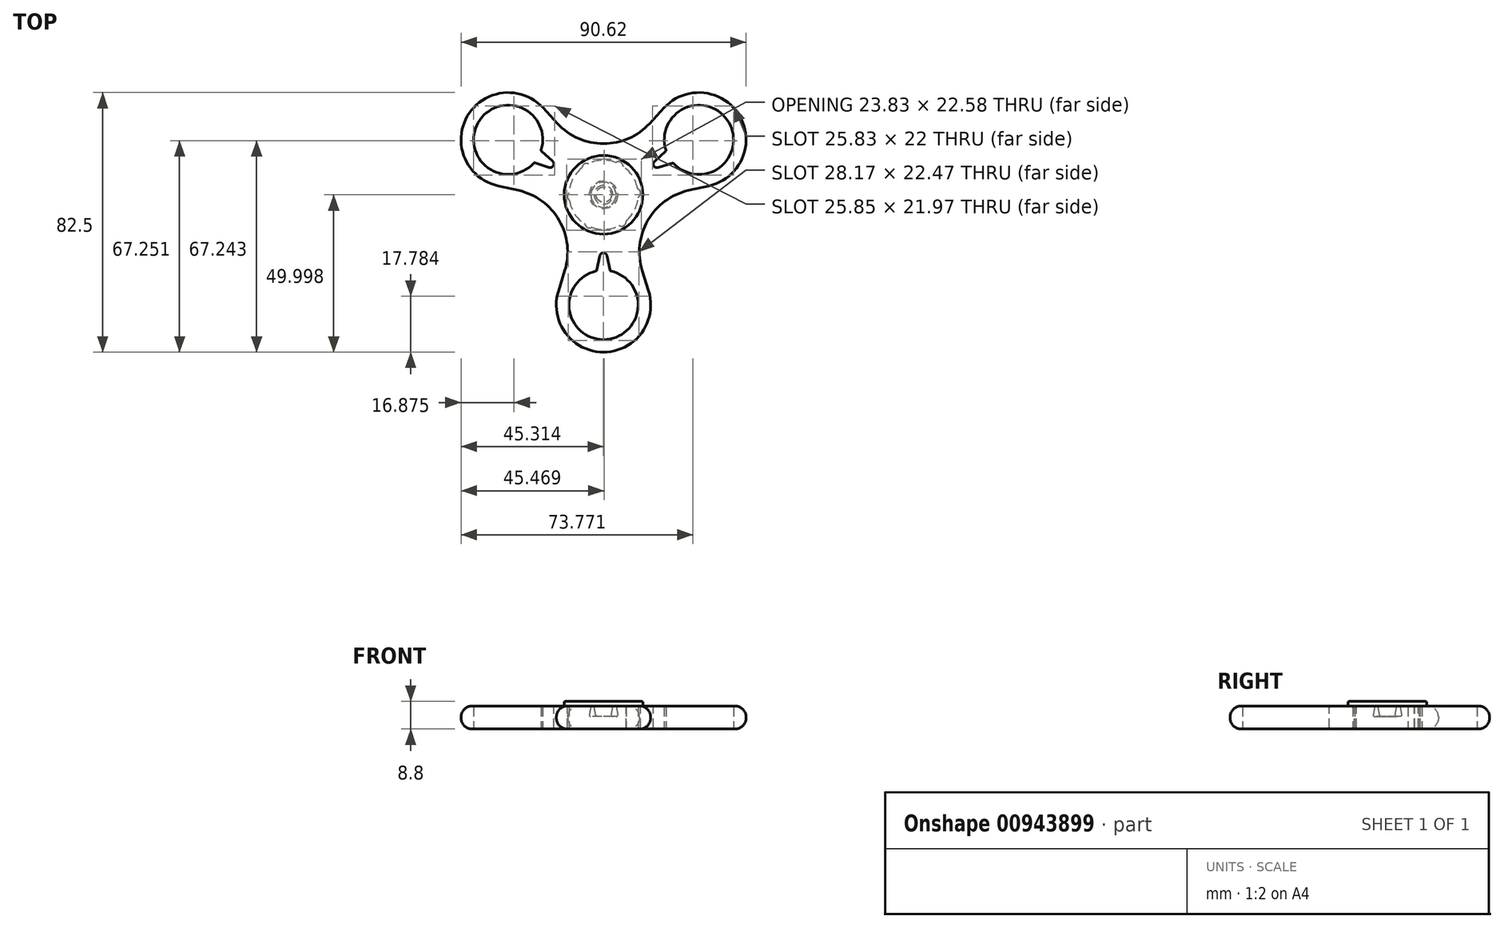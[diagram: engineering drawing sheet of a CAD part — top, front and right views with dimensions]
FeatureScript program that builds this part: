
annotation { "Feature Type Name" : "Feature", "Feature Type Description" : "" }
export const myFeature = defineFeature(function(context is Context, id is Id, definition is map)
    precondition{}
    {
        {
            var Q0;
            Q0=qCreatedBy(makeId("Top.planeOp"),FACE);
            var sketch = newSketch(context, id + "F0", { "sketchPlane" : qUnion([Q0])});
            skCircle(sketch, "E0", {"center": v(0, 0) * mm, "radius": 11 * mm});
            skCircle(sketch, "E1.cCircle", {"center": v(0, 0) * mm, "radius": 30.31 * mm, "construction": true});
            skLineSegment(sketch, "E1.0", {"start": v(0, 35) * mm, "end": v(30.31, 17.5) * mm, "construction": true});
            skLineSegment(sketch, "E1.1", {"start": v(30.31, 17.5) * mm, "end": v(30.31, -17.5) * mm, "construction": true});
            skLineSegment(sketch, "E1.2", {"start": v(30.31, -17.5) * mm, "end": v(0, -35) * mm, "construction": true});
            skLineSegment(sketch, "E1.3", {"start": v(0, -35) * mm, "end": v(-30.31, -17.5) * mm, "construction": true});
            skLineSegment(sketch, "E1.4", {"start": v(-30.31, -17.5) * mm, "end": v(-30.31, 17.5) * mm, "construction": true});
            skLineSegment(sketch, "E1.5", {"start": v(-30.31, 17.5) * mm, "end": v(0, 35) * mm, "construction": true});
            skPoint(sketch, "E1.0.midPoint", {"position": v(15.16, 26.25) * mm});
            skLineSegment(sketch, "E2", {"start": v(0, 0) * mm, "end": v(30.31, 17.5) * mm, "construction": true});
            skLineSegment(sketch, "E3", {"start": v(0, 0) * mm, "end": v(-30.31, 17.5) * mm, "construction": true});
            skLineSegment(sketch, "E4", {"start": v(0, 0) * mm, "end": v(0, -35) * mm, "construction": true});
            skCircle(sketch, "E5", {"center": v(-30.31, 17.5) * mm, "radius": 11 * mm});
            skCircle(sketch, "E6", {"center": v(30.31, 17.5) * mm, "radius": 11 * mm});
            skCircle(sketch, "E7", {"center": v(0, -35) * mm, "radius": 11 * mm});
            skArc(sketch, "E8", {"start": v(-12.3, -24.08) * mm, "mid": v(-11.52, -15.92) * mm, "end": v(-14.08, -8.13) * mm});
            skLineSegment(sketch, "E9", {"start": v(30.31, 17.5) * mm, "end": v(-30.31, -17.5) * mm, "construction": true});
            skArc(sketch, "E10", {"start": v(-14.32, -30.54) * mm, "mid": v(-12.08, -43.89) * mm, "end": v(0, -50) * mm});
            skLineSegment(sketch, "E11", {"start": v(-12.3, -24.08) * mm, "end": v(-14.32, -30.54) * mm});
            skArc(sketch, "E12.MirrorCS", {"start": v(14.32, -30.54) * mm, "mid": v(12.08, -43.89) * mm, "end": v(0, -50) * mm});
            skLineSegment(sketch, "E13.MirrorCS", {"start": v(12.3, -24.08) * mm, "end": v(14.32, -30.54) * mm});
            skArc(sketch, "E14.MirrorCS", {"start": v(12.3, -24.08) * mm, "mid": v(11.52, -15.92) * mm, "end": v(14.08, -8.13) * mm});
            skArc(sketch, "E15.1.0", {"start": v(14.7, 22.7) * mm, "mid": v(8.03, 17.94) * mm, "end": v(0, 16.26) * mm});
            skLineSegment(sketch, "E15.1.1", {"start": v(14.7, 22.7) * mm, "end": v(19.28, 27.67) * mm});
            skArc(sketch, "E15.1.2", {"start": v(19.28, 27.67) * mm, "mid": v(31.97, 32.4) * mm, "end": v(43.3, 25) * mm});
            skArc(sketch, "E15.1.3", {"start": v(33.6, 2.87) * mm, "mid": v(44.05, 11.48) * mm, "end": v(43.3, 25) * mm});
            skLineSegment(sketch, "E15.1.4", {"start": v(27.01, 1.38) * mm, "end": v(33.6, 2.87) * mm});
            skArc(sketch, "E15.1.5", {"start": v(27.01, 1.38) * mm, "mid": v(19.55, -2.02) * mm, "end": v(14.08, -8.13) * mm});
            skArc(sketch, "E15.2.0", {"start": v(-27.01, 1.38) * mm, "mid": v(-19.55, -2.02) * mm, "end": v(-14.08, -8.13) * mm});
            skLineSegment(sketch, "E15.2.1", {"start": v(-27.01, 1.38) * mm, "end": v(-33.6, 2.87) * mm});
            skArc(sketch, "E15.2.2", {"start": v(-33.6, 2.87) * mm, "mid": v(-44.05, 11.48) * mm, "end": v(-43.3, 25) * mm});
            skArc(sketch, "E15.2.3", {"start": v(-19.28, 27.67) * mm, "mid": v(-31.97, 32.4) * mm, "end": v(-43.3, 25) * mm});
            skLineSegment(sketch, "E15.2.4", {"start": v(-14.7, 22.7) * mm, "end": v(-19.28, 27.67) * mm});
            skArc(sketch, "E15.2.5", {"start": v(-14.7, 22.7) * mm, "mid": v(-8.03, 17.94) * mm, "end": v(0, 16.26) * mm});
            skSolve(sketch);
        }
        {
            var Q0;
            Q0 = qSketchRegion(id + "F0", true);
            extrude(context, id + "F1", {"entities" : qUnion([Q0]), "depth" : 7.3 * mm, "offsetDistance" : 25 * mm});
        }
        {
            var Q0;
            Q0=makeQuery(id+"F1.opExtrude","CAP_EDGE",EDGE,{"disambiguationData":[OSD([sQuery(id+"F0.wireOp",EDGE,"E15.2.2"),sQuery(id+"F0.wireOp",EDGE,"E15.2.3")])],"isStart":false});
            var Q1;
            Q1=makeQuery(id+"F1.opExtrude","CAP_EDGE",EDGE,{"disambiguationData":[OSD([sQuery(id+"F0.wireOp",EDGE,"E15.2.1")])],"isStart":true});
            fillet(context, id + "F2", {"entities" : qUnion([Q0, Q1]), "radius" : 3.5 * mm, "tangentPropagation" : true, "allowEdgeOverflow" : false});
        }
        {
            var Q0;
            Q0=makeQuery(id+"F1.opExtrude","CAP_FACE",FACE,{"disambiguationData":[OSD([sQuery(id+"F0.wireOp",EDGE,"E0"),sQuery(id+"F0.wireOp",EDGE,"E5"),sQuery(id+"F0.wireOp",EDGE,"E6"),sQuery(id+"F0.wireOp",EDGE,"E7"),sQuery(id+"F0.wireOp",EDGE,"E8"),sQuery(id+"F0.wireOp",EDGE,"E10"),sQuery(id+"F0.wireOp",EDGE,"E11"),sQuery(id+"F0.wireOp",EDGE,"E12.MirrorCS"),sQuery(id+"F0.wireOp",EDGE,"E13.MirrorCS"),sQuery(id+"F0.wireOp",EDGE,"E14.MirrorCS"),sQuery(id+"F0.wireOp",EDGE,"E15.1.0"),sQuery(id+"F0.wireOp",EDGE,"E15.1.1"),sQuery(id+"F0.wireOp",EDGE,"E15.1.2"),sQuery(id+"F0.wireOp",EDGE,"E15.1.3"),sQuery(id+"F0.wireOp",EDGE,"E15.1.4"),sQuery(id+"F0.wireOp",EDGE,"E15.1.5"),sQuery(id+"F0.wireOp",EDGE,"E15.2.0"),sQuery(id+"F0.wireOp",EDGE,"E15.2.1"),sQuery(id+"F0.wireOp",EDGE,"E15.2.2"),sQuery(id+"F0.wireOp",EDGE,"E15.2.3"),sQuery(id+"F0.wireOp",EDGE,"E15.2.4"),sQuery(id+"F0.wireOp",EDGE,"E15.2.5")])],"isStart":false});
            var sketch = newSketch(context, id + "F3", { "sketchPlane" : qUnion([Q0])});
            skCircle(sketch, "E16.0", {"center": v(0, 0) * mm, "radius": 11 * mm});
            skCircle(sketch, "E17", {"center": v(0, 0) * mm, "radius": 12.5 * mm});
            skCircle(sketch, "E18", {"center": v(0, 0) * mm, "radius": 4 * mm});
            skCircle(sketch, "E19", {"center": v(0, 0) * mm, "radius": 3 * mm});
            skSolve(sketch);
        }
        {
            var Q0;
            Q0=makeQuery(id+"F3.imprint","IMPRINT",FACE,{"disambiguationData":[TD([[makeQuery(id+"F3.imprint","IMPRINT",EDGE,{"derivedFrom":sQuery(id+"F3.wireOp",EDGE,"E19")}),1.0]])]});
            var Q1;
            Q1=makeQuery(id+"F3.imprint","IMPRINT",FACE,{"disambiguationData":[TD([[makeQuery(id+"F3.imprint","IMPRINT",EDGE,{"derivedFrom":sQuery(id+"F3.wireOp",EDGE,"E18")}),1.0]])]});
            var Q2;
            Q2=makeQuery(id+"F3.imprint","IMPRINT",FACE,{"disambiguationData":[TD([[makeQuery(id+"F3.imprint","IMPRINT",EDGE,{"derivedFrom":sQuery(id+"F3.wireOp",EDGE,"E16.0")}),1.0]])]});
            var Q3;
            Q3=makeQuery(id+"F3.imprint","IMPRINT",FACE,{"disambiguationData":[TD([[makeQuery(id+"F3.imprint","IMPRINT",EDGE,{"derivedFrom":sQuery(id+"F3.wireOp",EDGE,"E16.0")}),-1.0]])]});
            extrude(context, id + "F4", {"entities" : qUnion([Q0, Q1, Q2, Q3]), "depth" : 1.5 * mm, "offsetDistance" : 25 * mm});
        }
        {
            var Q0;
            Q0=makeQuery(id+"F3.imprint","IMPRINT",FACE,{"disambiguationData":[TD([[makeQuery(id+"F3.imprint","IMPRINT",EDGE,{"derivedFrom":sQuery(id+"F3.wireOp",EDGE,"E18")}),1.0]])]});
            extrude(context, id + "F5", {"entities" : qUnion([Q0]), "operationType" : NewBodyOperationType.ADD, "oppositeDirection" : true, "depth" : 3.3 * mm, "offsetDistance" : 25 * mm, "hasDraft" : true, "draftAngle" : 10 * degree});
        }
        {
            var Q0;
            Q0=makeQuery(id+"F5.opExtrude","CAP_FACE",FACE,{"disambiguationData":[OSD([sQuery(id+"F3.wireOp",EDGE,"E18"),sQuery(id+"F3.wireOp",EDGE,"E19")])],"isStart":false});
            var Q1;
            Q1=makeQuery(id+"F4.opExtrude","CAP_FACE",FACE,{"disambiguationData":[OSD([sQuery(id+"F3.wireOp",EDGE,"E17"),sQuery(id+"F3.wireOp",EDGE,"E19")])],"isStart":false});
            fillet(context, id + "F6", {"entities" : qUnion([Q0, Q1]), "radius" : 0.4 * mm, "tangentPropagation" : true, "allowEdgeOverflow" : false});
        }
        {
            var Q0;
            Q0=makeQuery(id+"F1.opExtrude","CAP_FACE",FACE,{"disambiguationData":[OSD([sQuery(id+"F0.wireOp",EDGE,"E0"),sQuery(id+"F0.wireOp",EDGE,"E5"),sQuery(id+"F0.wireOp",EDGE,"E6"),sQuery(id+"F0.wireOp",EDGE,"E7"),sQuery(id+"F0.wireOp",EDGE,"E8"),sQuery(id+"F0.wireOp",EDGE,"E10"),sQuery(id+"F0.wireOp",EDGE,"E11"),sQuery(id+"F0.wireOp",EDGE,"E12.MirrorCS"),sQuery(id+"F0.wireOp",EDGE,"E13.MirrorCS"),sQuery(id+"F0.wireOp",EDGE,"E14.MirrorCS"),sQuery(id+"F0.wireOp",EDGE,"E15.1.0"),sQuery(id+"F0.wireOp",EDGE,"E15.1.1"),sQuery(id+"F0.wireOp",EDGE,"E15.1.2"),sQuery(id+"F0.wireOp",EDGE,"E15.1.3"),sQuery(id+"F0.wireOp",EDGE,"E15.1.4"),sQuery(id+"F0.wireOp",EDGE,"E15.1.5"),sQuery(id+"F0.wireOp",EDGE,"E15.2.0"),sQuery(id+"F0.wireOp",EDGE,"E15.2.1"),sQuery(id+"F0.wireOp",EDGE,"E15.2.2"),sQuery(id+"F0.wireOp",EDGE,"E15.2.3"),sQuery(id+"F0.wireOp",EDGE,"E15.2.4"),sQuery(id+"F0.wireOp",EDGE,"E15.2.5")])],"isStart":false});
            var sketch = newSketch(context, id + "F7", { "sketchPlane" : qUnion([Q0])});
            skLineSegment(sketch, "E20", {"start": v(-30.53, 12.92) * mm, "end": v(-17.27, 8.73) * mm});
            skLineSegment(sketch, "E21", {"start": v(-16.16, 10.65) * mm, "end": v(-26.23, 19.89) * mm});
            skLineSegment(sketch, "E22", {"start": v(-26.23, 19.89) * mm, "end": v(-30.53, 12.92) * mm});
            skPoint(sketch, "E23.center", {"position": v(-0.34, 0.1) * mm});
            skArc(sketch, "E24", {"start": v(-17.27, 8.73) * mm, "mid": v(-15.95, 9.25) * mm, "end": v(-16.16, 10.65) * mm});
            skPoint(sketch, "E25.orphan", {"position": v(-12.39, 7.19) * mm});
            skLineSegment(sketch, "E26.1.0", {"start": v(-1.14, -19.32) * mm, "end": v(-4.11, -32.66) * mm});
            skArc(sketch, "E26.1.1", {"start": v(1.07, -19.32) * mm, "mid": v(-0.03, -18.43) * mm, "end": v(-1.14, -19.32) * mm});
            skLineSegment(sketch, "E26.1.2", {"start": v(4.07, -32.9) * mm, "end": v(1.07, -19.32) * mm});
            skLineSegment(sketch, "E26.1.3", {"start": v(-4.11, -32.66) * mm, "end": v(4.07, -32.9) * mm});
            skLineSegment(sketch, "E26.2.0", {"start": v(17.3, 8.67) * mm, "end": v(30.34, 12.77) * mm});
            skArc(sketch, "E26.2.1", {"start": v(16.2, 10.6) * mm, "mid": v(15.98, 9.19) * mm, "end": v(17.3, 8.67) * mm});
            skLineSegment(sketch, "E26.2.2", {"start": v(26.45, 19.98) * mm, "end": v(16.2, 10.6) * mm});
            skLineSegment(sketch, "E26.2.3", {"start": v(30.34, 12.77) * mm, "end": v(26.45, 19.98) * mm});
            skPoint(sketch, "E26.center", {"position": v(0, 0) * mm});
            skLineSegment(sketch, "E27", {"start": v(-0.34, 0.1) * mm, "end": v(5.49, 10.34) * mm, "construction": true});
            skArc(sketch, "E28", {"start": v(5.84, 8.03) * mm, "mid": v(6.22, 9.27) * mm, "end": v(5.49, 10.34) * mm});
            skLineSegment(sketch, "E29", {"start": v(5.84, 8.03) * mm, "end": v(4.54, 6.63) * mm});
            skArc(sketch, "E30.MirrorCS", {"start": v(3.32, 9.46) * mm, "mid": v(4.2, 10.42) * mm, "end": v(5.49, 10.34) * mm});
            skLineSegment(sketch, "E31.MirrorCS", {"start": v(3.32, 9.46) * mm, "end": v(2.78, 7.63) * mm});
            skLineSegment(sketch, "E32", {"start": v(2.78, 7.63) * mm, "end": v(4.54, 6.63) * mm});
            skLineSegment(sketch, "E33.1.0", {"start": v(-6.45, 7.47) * mm, "end": v(-5.13, 6.09) * mm});
            skArc(sketch, "E33.1.1", {"start": v(-6.45, 7.47) * mm, "mid": v(-6.85, 8.7) * mm, "end": v(-6.13, 9.78) * mm});
            skArc(sketch, "E33.1.2", {"start": v(-3.95, 8.94) * mm, "mid": v(-4.84, 9.89) * mm, "end": v(-6.13, 9.78) * mm});
            skLineSegment(sketch, "E33.1.3", {"start": v(-3.95, 8.94) * mm, "end": v(-3.4, 7.1) * mm});
            skLineSegment(sketch, "E33.1.4", {"start": v(-5.13, 6.09) * mm, "end": v(-3.4, 7.1) * mm});
            skLineSegment(sketch, "E33.1.5", {"start": v(-0.18, -0.38) * mm, "end": v(-6.13, 9.78) * mm, "construction": true});
            skLineSegment(sketch, "E33.2.0", {"start": v(-9.62, -2) * mm, "end": v(-7.76, -1.54) * mm});
            skArc(sketch, "E33.2.1", {"start": v(-9.62, -2) * mm, "mid": v(-10.88, -1.72) * mm, "end": v(-11.46, -0.55) * mm});
            skArc(sketch, "E33.2.2", {"start": v(-9.63, 0.9) * mm, "mid": v(-10.9, 0.62) * mm, "end": v(-11.46, -0.55) * mm});
            skLineSegment(sketch, "E33.2.3", {"start": v(-9.63, 0.9) * mm, "end": v(-7.77, 0.48) * mm});
            skLineSegment(sketch, "E33.2.4", {"start": v(-7.76, -1.54) * mm, "end": v(-7.77, 0.48) * mm});
            skLineSegment(sketch, "E33.2.5", {"start": v(0.32, -0.48) * mm, "end": v(-11.46, -0.55) * mm, "construction": true});
            skLineSegment(sketch, "E33.3.0", {"start": v(-3, -9.46) * mm, "end": v(-2.47, -7.63) * mm});
            skArc(sketch, "E33.3.1", {"start": v(-3, -9.46) * mm, "mid": v(-3.87, -10.42) * mm, "end": v(-5.17, -10.34) * mm});
            skArc(sketch, "E33.3.2", {"start": v(-5.52, -8.03) * mm, "mid": v(-5.9, -9.27) * mm, "end": v(-5.17, -10.34) * mm});
            skLineSegment(sketch, "E33.3.3", {"start": v(-5.52, -8.03) * mm, "end": v(-4.22, -6.63) * mm});
            skLineSegment(sketch, "E33.3.4", {"start": v(-2.47, -7.63) * mm, "end": v(-4.22, -6.63) * mm});
            skLineSegment(sketch, "E33.3.5", {"start": v(0.65, -0.1) * mm, "end": v(-5.17, -10.34) * mm, "construction": true});
            skLineSegment(sketch, "E33.4.0", {"start": v(6.77, -7.47) * mm, "end": v(5.45, -6.09) * mm});
            skArc(sketch, "E33.4.1", {"start": v(6.77, -7.47) * mm, "mid": v(7.17, -8.7) * mm, "end": v(6.45, -9.78) * mm});
            skArc(sketch, "E33.4.2", {"start": v(4.27, -8.93) * mm, "mid": v(5.15, -9.88) * mm, "end": v(6.45, -9.78) * mm});
            skLineSegment(sketch, "E33.4.3", {"start": v(4.27, -8.93) * mm, "end": v(3.7, -7.1) * mm});
            skLineSegment(sketch, "E33.4.4", {"start": v(5.45, -6.09) * mm, "end": v(3.7, -7.1) * mm});
            skLineSegment(sketch, "E33.4.5", {"start": v(0.5, 0.38) * mm, "end": v(6.45, -9.78) * mm, "construction": true});
            skLineSegment(sketch, "E33.5.0", {"start": v(9.93, 2) * mm, "end": v(8.08, 1.54) * mm});
            skArc(sketch, "E33.5.1", {"start": v(9.93, 2) * mm, "mid": v(11.2, 1.72) * mm, "end": v(11.77, 0.55) * mm});
            skArc(sketch, "E33.5.2", {"start": v(9.95, -0.9) * mm, "mid": v(11.22, -0.62) * mm, "end": v(11.77, 0.55) * mm});
            skLineSegment(sketch, "E33.5.3", {"start": v(9.95, -0.9) * mm, "end": v(8.09, -0.48) * mm});
            skLineSegment(sketch, "E33.5.4", {"start": v(8.08, 1.54) * mm, "end": v(8.09, -0.48) * mm});
            skLineSegment(sketch, "E33.5.5", {"start": v(0, 0.48) * mm, "end": v(11.77, 0.55) * mm, "construction": true});
            skPoint(sketch, "E33.center", {"position": v(0.16, 0) * mm});
            skSolve(sketch);
        }
        {
            var Q0;
            Q0 = qSketchRegion(id + "F7", true);
            extrude(context, id + "F8", {"entities" : qUnion([Q0]), "operationType" : NewBodyOperationType.REMOVE, "oppositeDirection" : true, "depth" : 25 * mm, "offsetDistance" : 25 * mm});
        }
        {
            var Q0;
            Q0=makeQuery(id+"F1.opExtrude","CAP_FACE",FACE,{"disambiguationData":[OSD([sQuery(id+"F0.wireOp",EDGE,"E0"),sQuery(id+"F0.wireOp",EDGE,"E5"),sQuery(id+"F0.wireOp",EDGE,"E6"),sQuery(id+"F0.wireOp",EDGE,"E7"),sQuery(id+"F0.wireOp",EDGE,"E8"),sQuery(id+"F0.wireOp",EDGE,"E10"),sQuery(id+"F0.wireOp",EDGE,"E11"),sQuery(id+"F0.wireOp",EDGE,"E12.MirrorCS"),sQuery(id+"F0.wireOp",EDGE,"E13.MirrorCS"),sQuery(id+"F0.wireOp",EDGE,"E14.MirrorCS"),sQuery(id+"F0.wireOp",EDGE,"E15.1.0"),sQuery(id+"F0.wireOp",EDGE,"E15.1.1"),sQuery(id+"F0.wireOp",EDGE,"E15.1.2"),sQuery(id+"F0.wireOp",EDGE,"E15.1.3"),sQuery(id+"F0.wireOp",EDGE,"E15.1.4"),sQuery(id+"F0.wireOp",EDGE,"E15.1.5"),sQuery(id+"F0.wireOp",EDGE,"E15.2.0"),sQuery(id+"F0.wireOp",EDGE,"E15.2.1"),sQuery(id+"F0.wireOp",EDGE,"E15.2.2"),sQuery(id+"F0.wireOp",EDGE,"E15.2.3"),sQuery(id+"F0.wireOp",EDGE,"E15.2.4"),sQuery(id+"F0.wireOp",EDGE,"E15.2.5")])],"isStart":false});
            var Q1;
            Q1=makeQuery(id+"F1.opExtrude","CAP_FACE",FACE,{"disambiguationData":[OSD([sQuery(id+"F0.wireOp",EDGE,"E0"),sQuery(id+"F0.wireOp",EDGE,"E5"),sQuery(id+"F0.wireOp",EDGE,"E6"),sQuery(id+"F0.wireOp",EDGE,"E7"),sQuery(id+"F0.wireOp",EDGE,"E8"),sQuery(id+"F0.wireOp",EDGE,"E10"),sQuery(id+"F0.wireOp",EDGE,"E11"),sQuery(id+"F0.wireOp",EDGE,"E12.MirrorCS"),sQuery(id+"F0.wireOp",EDGE,"E13.MirrorCS"),sQuery(id+"F0.wireOp",EDGE,"E14.MirrorCS"),sQuery(id+"F0.wireOp",EDGE,"E15.1.0"),sQuery(id+"F0.wireOp",EDGE,"E15.1.1"),sQuery(id+"F0.wireOp",EDGE,"E15.1.2"),sQuery(id+"F0.wireOp",EDGE,"E15.1.3"),sQuery(id+"F0.wireOp",EDGE,"E15.1.4"),sQuery(id+"F0.wireOp",EDGE,"E15.1.5"),sQuery(id+"F0.wireOp",EDGE,"E15.2.0"),sQuery(id+"F0.wireOp",EDGE,"E15.2.1"),sQuery(id+"F0.wireOp",EDGE,"E15.2.2"),sQuery(id+"F0.wireOp",EDGE,"E15.2.3"),sQuery(id+"F0.wireOp",EDGE,"E15.2.4"),sQuery(id+"F0.wireOp",EDGE,"E15.2.5")])],"isStart":true});
            var Q2;
            Q2=makeQuery(id+"F1.opExtrude","SWEPT_FACE",FACE,{"disambiguationData":[OSD([sQuery(id+"F0.wireOp",EDGE,"E5")])]});
            var Q3;
            Q3=makeQuery(id+"F1.opExtrude","SWEPT_FACE",FACE,{"disambiguationData":[OSD([sQuery(id+"F0.wireOp",EDGE,"E6")])]});
            var Q4;
            {var subQ0=sQuery(id+"F0.wireOp",EDGE,"E15.2.5");var subQ1=sQuery(id+"F0.wireOp",EDGE,"E15.2.4");var subQ2=sQuery(id+"F0.wireOp",EDGE,"E15.2.3");var subQ3=sQuery(id+"F0.wireOp",EDGE,"E15.2.2");var subQ4=sQuery(id+"F0.wireOp",EDGE,"E15.2.1");var subQ5=sQuery(id+"F0.wireOp",EDGE,"E15.2.0");var subQ6=sQuery(id+"F0.wireOp",EDGE,"E15.1.5");var subQ7=sQuery(id+"F0.wireOp",EDGE,"E15.1.4");var subQ8=sQuery(id+"F0.wireOp",EDGE,"E15.1.3");var subQ9=sQuery(id+"F0.wireOp",EDGE,"E15.1.2");var subQ10=sQuery(id+"F0.wireOp",EDGE,"E15.1.1");var subQ11=sQuery(id+"F0.wireOp",EDGE,"E15.1.0");var subQ12=sQuery(id+"F0.wireOp",EDGE,"E14.MirrorCS");var subQ13=sQuery(id+"F0.wireOp",EDGE,"E13.MirrorCS");var subQ14=sQuery(id+"F0.wireOp",EDGE,"E12.MirrorCS");var subQ15=sQuery(id+"F0.wireOp",EDGE,"E11");var subQ16=sQuery(id+"F0.wireOp",EDGE,"E10");var subQ17=sQuery(id+"F0.wireOp",EDGE,"E8");var subQ18=sQuery(id+"F0.wireOp",EDGE,"E7");var subQ19=sQuery(id+"F0.wireOp",EDGE,"E6");var subQ20=sQuery(id+"F0.wireOp",EDGE,"E5");var subQ21=sQuery(id+"F0.wireOp",EDGE,"E0");Q4=makeQuery(id+"F8.boolean.opBoolean","SPLIT",FACE,{"disambiguationData":[TD([makeQuery(id+"F1.opExtrude","CAP_FACE",FACE,{"disambiguationData":[OSD([subQ21,subQ20,subQ19,subQ18,subQ17,subQ16,subQ15,subQ14,subQ13,subQ12,subQ11,subQ10,subQ9,subQ8,subQ7,subQ6,subQ5,subQ4,subQ3,subQ2,subQ1,subQ0])],"isStart":true}),makeQuery(id+"F1.opExtrude","CAP_FACE",FACE,{"disambiguationData":[OSD([subQ21,subQ20,subQ19,subQ18,subQ17,subQ16,subQ15,subQ14,subQ13,subQ12,subQ11,subQ10,subQ9,subQ8,subQ7,subQ6,subQ5,subQ4,subQ3,subQ2,subQ1,subQ0])],"isStart":false}),makeQuery(id+"F8.opExtrude","SWEPT_FACE",FACE,{"disambiguationData":[OSD([sQuery(id+"F7.wireOp",EDGE,"E33.4.1"),sQuery(id+"F7.wireOp",EDGE,"E33.4.2")])]}),makeQuery(id+"F8.opExtrude","SWEPT_FACE",FACE,{"disambiguationData":[OSD([sQuery(id+"F7.wireOp",EDGE,"E33.5.1"),sQuery(id+"F7.wireOp",EDGE,"E33.5.2")])]})])],"derivedFrom":makeQuery(id+"F1.opExtrude","SWEPT_FACE",FACE,{"disambiguationData":[OSD([subQ21])]})});}
            var Q5;
            Q5=makeQuery(id+"F1.opExtrude","SWEPT_FACE",FACE,{"disambiguationData":[OSD([sQuery(id+"F0.wireOp",EDGE,"E7")])]});
            var Q6;
            {var subQ0=sQuery(id+"F0.wireOp",EDGE,"E15.2.5");var subQ1=sQuery(id+"F0.wireOp",EDGE,"E15.2.4");var subQ2=sQuery(id+"F0.wireOp",EDGE,"E15.2.3");var subQ3=sQuery(id+"F0.wireOp",EDGE,"E15.2.2");var subQ4=sQuery(id+"F0.wireOp",EDGE,"E15.2.1");var subQ5=sQuery(id+"F0.wireOp",EDGE,"E15.2.0");var subQ6=sQuery(id+"F0.wireOp",EDGE,"E15.1.5");var subQ7=sQuery(id+"F0.wireOp",EDGE,"E15.1.4");var subQ8=sQuery(id+"F0.wireOp",EDGE,"E15.1.3");var subQ9=sQuery(id+"F0.wireOp",EDGE,"E15.1.2");var subQ10=sQuery(id+"F0.wireOp",EDGE,"E15.1.1");var subQ11=sQuery(id+"F0.wireOp",EDGE,"E15.1.0");var subQ12=sQuery(id+"F0.wireOp",EDGE,"E14.MirrorCS");var subQ13=sQuery(id+"F0.wireOp",EDGE,"E13.MirrorCS");var subQ14=sQuery(id+"F0.wireOp",EDGE,"E12.MirrorCS");var subQ15=sQuery(id+"F0.wireOp",EDGE,"E11");var subQ16=sQuery(id+"F0.wireOp",EDGE,"E10");var subQ17=sQuery(id+"F0.wireOp",EDGE,"E8");var subQ18=sQuery(id+"F0.wireOp",EDGE,"E7");var subQ19=sQuery(id+"F0.wireOp",EDGE,"E6");var subQ20=sQuery(id+"F0.wireOp",EDGE,"E5");var subQ21=sQuery(id+"F0.wireOp",EDGE,"E0");Q6=makeQuery(id+"F8.boolean.opBoolean","SPLIT",FACE,{"disambiguationData":[TD([makeQuery(id+"F1.opExtrude","CAP_FACE",FACE,{"disambiguationData":[OSD([subQ21,subQ20,subQ19,subQ18,subQ17,subQ16,subQ15,subQ14,subQ13,subQ12,subQ11,subQ10,subQ9,subQ8,subQ7,subQ6,subQ5,subQ4,subQ3,subQ2,subQ1,subQ0])],"isStart":true}),makeQuery(id+"F1.opExtrude","CAP_FACE",FACE,{"disambiguationData":[OSD([subQ21,subQ20,subQ19,subQ18,subQ17,subQ16,subQ15,subQ14,subQ13,subQ12,subQ11,subQ10,subQ9,subQ8,subQ7,subQ6,subQ5,subQ4,subQ3,subQ2,subQ1,subQ0])],"isStart":false}),makeQuery(id+"F8.opExtrude","SWEPT_FACE",FACE,{"disambiguationData":[OSD([sQuery(id+"F7.wireOp",EDGE,"E33.3.1"),sQuery(id+"F7.wireOp",EDGE,"E33.3.2")])]}),makeQuery(id+"F8.opExtrude","SWEPT_FACE",FACE,{"disambiguationData":[OSD([sQuery(id+"F7.wireOp",EDGE,"E33.4.1"),sQuery(id+"F7.wireOp",EDGE,"E33.4.2")])]})])],"derivedFrom":makeQuery(id+"F1.opExtrude","SWEPT_FACE",FACE,{"disambiguationData":[OSD([subQ21])]})});}
            var Q7;
            {var subQ0=sQuery(id+"F0.wireOp",EDGE,"E15.2.5");var subQ1=sQuery(id+"F0.wireOp",EDGE,"E15.2.4");var subQ2=sQuery(id+"F0.wireOp",EDGE,"E15.2.3");var subQ3=sQuery(id+"F0.wireOp",EDGE,"E15.2.2");var subQ4=sQuery(id+"F0.wireOp",EDGE,"E15.2.1");var subQ5=sQuery(id+"F0.wireOp",EDGE,"E15.2.0");var subQ6=sQuery(id+"F0.wireOp",EDGE,"E15.1.5");var subQ7=sQuery(id+"F0.wireOp",EDGE,"E15.1.4");var subQ8=sQuery(id+"F0.wireOp",EDGE,"E15.1.3");var subQ9=sQuery(id+"F0.wireOp",EDGE,"E15.1.2");var subQ10=sQuery(id+"F0.wireOp",EDGE,"E15.1.1");var subQ11=sQuery(id+"F0.wireOp",EDGE,"E15.1.0");var subQ12=sQuery(id+"F0.wireOp",EDGE,"E14.MirrorCS");var subQ13=sQuery(id+"F0.wireOp",EDGE,"E13.MirrorCS");var subQ14=sQuery(id+"F0.wireOp",EDGE,"E12.MirrorCS");var subQ15=sQuery(id+"F0.wireOp",EDGE,"E11");var subQ16=sQuery(id+"F0.wireOp",EDGE,"E10");var subQ17=sQuery(id+"F0.wireOp",EDGE,"E8");var subQ18=sQuery(id+"F0.wireOp",EDGE,"E7");var subQ19=sQuery(id+"F0.wireOp",EDGE,"E6");var subQ20=sQuery(id+"F0.wireOp",EDGE,"E5");var subQ21=sQuery(id+"F0.wireOp",EDGE,"E0");Q7=makeQuery(id+"F8.boolean.opBoolean","SPLIT",FACE,{"disambiguationData":[TD([makeQuery(id+"F1.opExtrude","CAP_FACE",FACE,{"disambiguationData":[OSD([subQ21,subQ20,subQ19,subQ18,subQ17,subQ16,subQ15,subQ14,subQ13,subQ12,subQ11,subQ10,subQ9,subQ8,subQ7,subQ6,subQ5,subQ4,subQ3,subQ2,subQ1,subQ0])],"isStart":true}),makeQuery(id+"F1.opExtrude","CAP_FACE",FACE,{"disambiguationData":[OSD([subQ21,subQ20,subQ19,subQ18,subQ17,subQ16,subQ15,subQ14,subQ13,subQ12,subQ11,subQ10,subQ9,subQ8,subQ7,subQ6,subQ5,subQ4,subQ3,subQ2,subQ1,subQ0])],"isStart":false}),makeQuery(id+"F8.opExtrude","SWEPT_FACE",FACE,{"disambiguationData":[OSD([sQuery(id+"F7.wireOp",EDGE,"E33.2.1"),sQuery(id+"F7.wireOp",EDGE,"E33.2.2")])]}),makeQuery(id+"F8.opExtrude","SWEPT_FACE",FACE,{"disambiguationData":[OSD([sQuery(id+"F7.wireOp",EDGE,"E33.3.1"),sQuery(id+"F7.wireOp",EDGE,"E33.3.2")])]})])],"derivedFrom":makeQuery(id+"F1.opExtrude","SWEPT_FACE",FACE,{"disambiguationData":[OSD([subQ21])]})});}
            var Q8;
            {var subQ0=sQuery(id+"F0.wireOp",EDGE,"E15.2.5");var subQ1=sQuery(id+"F0.wireOp",EDGE,"E15.2.4");var subQ2=sQuery(id+"F0.wireOp",EDGE,"E15.2.3");var subQ3=sQuery(id+"F0.wireOp",EDGE,"E15.2.2");var subQ4=sQuery(id+"F0.wireOp",EDGE,"E15.2.1");var subQ5=sQuery(id+"F0.wireOp",EDGE,"E15.2.0");var subQ6=sQuery(id+"F0.wireOp",EDGE,"E15.1.5");var subQ7=sQuery(id+"F0.wireOp",EDGE,"E15.1.4");var subQ8=sQuery(id+"F0.wireOp",EDGE,"E15.1.3");var subQ9=sQuery(id+"F0.wireOp",EDGE,"E15.1.2");var subQ10=sQuery(id+"F0.wireOp",EDGE,"E15.1.1");var subQ11=sQuery(id+"F0.wireOp",EDGE,"E15.1.0");var subQ12=sQuery(id+"F0.wireOp",EDGE,"E14.MirrorCS");var subQ13=sQuery(id+"F0.wireOp",EDGE,"E13.MirrorCS");var subQ14=sQuery(id+"F0.wireOp",EDGE,"E12.MirrorCS");var subQ15=sQuery(id+"F0.wireOp",EDGE,"E11");var subQ16=sQuery(id+"F0.wireOp",EDGE,"E10");var subQ17=sQuery(id+"F0.wireOp",EDGE,"E8");var subQ18=sQuery(id+"F0.wireOp",EDGE,"E7");var subQ19=sQuery(id+"F0.wireOp",EDGE,"E6");var subQ20=sQuery(id+"F0.wireOp",EDGE,"E5");var subQ21=sQuery(id+"F0.wireOp",EDGE,"E0");Q8=makeQuery(id+"F8.boolean.opBoolean","SPLIT",FACE,{"disambiguationData":[TD([makeQuery(id+"F1.opExtrude","CAP_FACE",FACE,{"disambiguationData":[OSD([subQ21,subQ20,subQ19,subQ18,subQ17,subQ16,subQ15,subQ14,subQ13,subQ12,subQ11,subQ10,subQ9,subQ8,subQ7,subQ6,subQ5,subQ4,subQ3,subQ2,subQ1,subQ0])],"isStart":true}),makeQuery(id+"F1.opExtrude","CAP_FACE",FACE,{"disambiguationData":[OSD([subQ21,subQ20,subQ19,subQ18,subQ17,subQ16,subQ15,subQ14,subQ13,subQ12,subQ11,subQ10,subQ9,subQ8,subQ7,subQ6,subQ5,subQ4,subQ3,subQ2,subQ1,subQ0])],"isStart":false}),makeQuery(id+"F8.opExtrude","SWEPT_FACE",FACE,{"disambiguationData":[OSD([sQuery(id+"F7.wireOp",EDGE,"E33.1.1"),sQuery(id+"F7.wireOp",EDGE,"E33.1.2")])]}),makeQuery(id+"F8.opExtrude","SWEPT_FACE",FACE,{"disambiguationData":[OSD([sQuery(id+"F7.wireOp",EDGE,"E33.2.1"),sQuery(id+"F7.wireOp",EDGE,"E33.2.2")])]})])],"derivedFrom":makeQuery(id+"F1.opExtrude","SWEPT_FACE",FACE,{"disambiguationData":[OSD([subQ21])]})});}
            var Q9;
            {var subQ0=sQuery(id+"F0.wireOp",EDGE,"E15.2.5");var subQ1=sQuery(id+"F0.wireOp",EDGE,"E15.2.4");var subQ2=sQuery(id+"F0.wireOp",EDGE,"E15.2.3");var subQ3=sQuery(id+"F0.wireOp",EDGE,"E15.2.2");var subQ4=sQuery(id+"F0.wireOp",EDGE,"E15.2.1");var subQ5=sQuery(id+"F0.wireOp",EDGE,"E15.2.0");var subQ6=sQuery(id+"F0.wireOp",EDGE,"E15.1.5");var subQ7=sQuery(id+"F0.wireOp",EDGE,"E15.1.4");var subQ8=sQuery(id+"F0.wireOp",EDGE,"E15.1.3");var subQ9=sQuery(id+"F0.wireOp",EDGE,"E15.1.2");var subQ10=sQuery(id+"F0.wireOp",EDGE,"E15.1.1");var subQ11=sQuery(id+"F0.wireOp",EDGE,"E15.1.0");var subQ12=sQuery(id+"F0.wireOp",EDGE,"E14.MirrorCS");var subQ13=sQuery(id+"F0.wireOp",EDGE,"E13.MirrorCS");var subQ14=sQuery(id+"F0.wireOp",EDGE,"E12.MirrorCS");var subQ15=sQuery(id+"F0.wireOp",EDGE,"E11");var subQ16=sQuery(id+"F0.wireOp",EDGE,"E10");var subQ17=sQuery(id+"F0.wireOp",EDGE,"E8");var subQ18=sQuery(id+"F0.wireOp",EDGE,"E7");var subQ19=sQuery(id+"F0.wireOp",EDGE,"E6");var subQ20=sQuery(id+"F0.wireOp",EDGE,"E5");var subQ21=sQuery(id+"F0.wireOp",EDGE,"E0");Q9=makeQuery(id+"F8.boolean.opBoolean","SPLIT",FACE,{"disambiguationData":[TD([makeQuery(id+"F1.opExtrude","CAP_FACE",FACE,{"disambiguationData":[OSD([subQ21,subQ20,subQ19,subQ18,subQ17,subQ16,subQ15,subQ14,subQ13,subQ12,subQ11,subQ10,subQ9,subQ8,subQ7,subQ6,subQ5,subQ4,subQ3,subQ2,subQ1,subQ0])],"isStart":true}),makeQuery(id+"F1.opExtrude","CAP_FACE",FACE,{"disambiguationData":[OSD([subQ21,subQ20,subQ19,subQ18,subQ17,subQ16,subQ15,subQ14,subQ13,subQ12,subQ11,subQ10,subQ9,subQ8,subQ7,subQ6,subQ5,subQ4,subQ3,subQ2,subQ1,subQ0])],"isStart":false}),makeQuery(id+"F8.opExtrude","SWEPT_FACE",FACE,{"disambiguationData":[OSD([sQuery(id+"F7.wireOp",EDGE,"E28"),sQuery(id+"F7.wireOp",EDGE,"E30.MirrorCS")])]}),makeQuery(id+"F8.opExtrude","SWEPT_FACE",FACE,{"disambiguationData":[OSD([sQuery(id+"F7.wireOp",EDGE,"E33.1.1"),sQuery(id+"F7.wireOp",EDGE,"E33.1.2")])]})])],"derivedFrom":makeQuery(id+"F1.opExtrude","SWEPT_FACE",FACE,{"disambiguationData":[OSD([subQ21])]})});}
            var Q10;
            {var subQ0=sQuery(id+"F0.wireOp",EDGE,"E15.2.5");var subQ1=sQuery(id+"F0.wireOp",EDGE,"E15.2.4");var subQ2=sQuery(id+"F0.wireOp",EDGE,"E15.2.3");var subQ3=sQuery(id+"F0.wireOp",EDGE,"E15.2.2");var subQ4=sQuery(id+"F0.wireOp",EDGE,"E15.2.1");var subQ5=sQuery(id+"F0.wireOp",EDGE,"E15.2.0");var subQ6=sQuery(id+"F0.wireOp",EDGE,"E15.1.5");var subQ7=sQuery(id+"F0.wireOp",EDGE,"E15.1.4");var subQ8=sQuery(id+"F0.wireOp",EDGE,"E15.1.3");var subQ9=sQuery(id+"F0.wireOp",EDGE,"E15.1.2");var subQ10=sQuery(id+"F0.wireOp",EDGE,"E15.1.1");var subQ11=sQuery(id+"F0.wireOp",EDGE,"E15.1.0");var subQ12=sQuery(id+"F0.wireOp",EDGE,"E14.MirrorCS");var subQ13=sQuery(id+"F0.wireOp",EDGE,"E13.MirrorCS");var subQ14=sQuery(id+"F0.wireOp",EDGE,"E12.MirrorCS");var subQ15=sQuery(id+"F0.wireOp",EDGE,"E11");var subQ16=sQuery(id+"F0.wireOp",EDGE,"E10");var subQ17=sQuery(id+"F0.wireOp",EDGE,"E8");var subQ18=sQuery(id+"F0.wireOp",EDGE,"E7");var subQ19=sQuery(id+"F0.wireOp",EDGE,"E6");var subQ20=sQuery(id+"F0.wireOp",EDGE,"E5");var subQ21=sQuery(id+"F0.wireOp",EDGE,"E0");Q10=makeQuery(id+"F8.boolean.opBoolean","SPLIT",FACE,{"disambiguationData":[TD([makeQuery(id+"F1.opExtrude","CAP_FACE",FACE,{"disambiguationData":[OSD([subQ21,subQ20,subQ19,subQ18,subQ17,subQ16,subQ15,subQ14,subQ13,subQ12,subQ11,subQ10,subQ9,subQ8,subQ7,subQ6,subQ5,subQ4,subQ3,subQ2,subQ1,subQ0])],"isStart":true}),makeQuery(id+"F1.opExtrude","CAP_FACE",FACE,{"disambiguationData":[OSD([subQ21,subQ20,subQ19,subQ18,subQ17,subQ16,subQ15,subQ14,subQ13,subQ12,subQ11,subQ10,subQ9,subQ8,subQ7,subQ6,subQ5,subQ4,subQ3,subQ2,subQ1,subQ0])],"isStart":false}),makeQuery(id+"F8.opExtrude","SWEPT_FACE",FACE,{"disambiguationData":[OSD([sQuery(id+"F7.wireOp",EDGE,"E28"),sQuery(id+"F7.wireOp",EDGE,"E30.MirrorCS")])]}),makeQuery(id+"F8.opExtrude","SWEPT_FACE",FACE,{"disambiguationData":[OSD([sQuery(id+"F7.wireOp",EDGE,"E33.5.1"),sQuery(id+"F7.wireOp",EDGE,"E33.5.2")])]})])],"derivedFrom":makeQuery(id+"F1.opExtrude","SWEPT_FACE",FACE,{"disambiguationData":[OSD([subQ21])]})});}
            fillet(context, id + "F9", {"entities" : qUnion([Q0, Q1, Q2, Q3, Q4, Q5, Q6, Q7, Q8, Q9, Q10]), "radius" : 0.3 * mm, "tangentPropagation" : true, "allowEdgeOverflow" : false});
        }
    });
